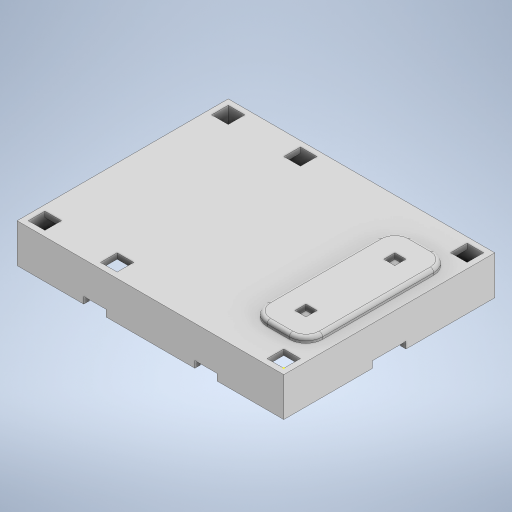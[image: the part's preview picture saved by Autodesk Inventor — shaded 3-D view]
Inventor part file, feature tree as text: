
AUTODESK INVENTOR PART (.ipt)
format: ipt  version: 2023 (Build 270158000, 158)  size: 404,992 bytes
history: native  units: mm
features: extrude x7, sketch x7, fillet x2
ambient origin geometry x8: Origin, YZ Plane, XZ Plane, XY Plane, X Axis, Y Axis, Z Axis, Center Point
bodies: Solid1 (feature_tree)
feature tree (16):
  extrude  "Extrusion1"  Depth=230.0mm
  extrude  "Extrusion2"  Depth=5.0mm
  extrude  "Extrusion3"  Depth=5.0mm
  extrude  "Extrusion4"  Depth=75.0mm
  fillet  "Fillet1"  Radius=75.0mm
  fillet  "Fillet2"  Radius=20.0mm
  extrude  "Extrusion5"  Depth=20.0mm
  extrude  "Extrusion6"  Depth=55.0mm
  extrude  "Extrusion7"  Depth=20.0mm
  sketch  "Sketch8"  dims[d16=55.0mm d17=20.0mm d18=80.0mm d19=6.0mm d20=0.0mm d21=24.0mm d22=0.0mm d23=5.0mm d24=0.0mm d25=130.0mm d26=30.0mm d27=30.0mm d28=10.0mm d29=50.0mm d30=5.0mm d31=0.0mm d32=15.0mm d33=3.0mm d34=10.0mm d35=10.0mm d36=20.0mm d37=20.0mm d40=10.0mm d41=10.0mm d42=20.0mm d43=20.0mm d44=5.0mm d45=0.0mm d46=15.0mm d47=15.0mm d51=15.0mm d52=15.0mm d53=15.0mm d54=15.0mm d55=15.0mm d56=15.0mm d57=15.0mm d58=15.0mm d59=50.0mm d60=5.0mm d61=0.0mm d62=5.0mm d63=0.0mm d64=15.0mm d65=15.0mm]
  sketch  "Sketch1"  dims[d0=180.0mm d1=230.0mm]
  sketch  "Sketch2"  dims[d2=5.0mm d3=5.0mm]
  sketch  "Sketch3"  dims[d4=5.0mm d5=5.0mm]
  sketch  "Sketch4"  dims[d6=30.0mm d7=75.0mm d8=75.0mm d9=20.0mm]
  sketch  "Sketch5"  dims[d10=20.0mm d12=20.0mm]
  sketch  "Sketch7"  dims[d14=80.0mm d15=55.0mm]
